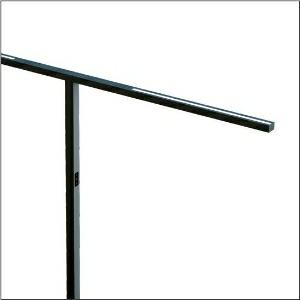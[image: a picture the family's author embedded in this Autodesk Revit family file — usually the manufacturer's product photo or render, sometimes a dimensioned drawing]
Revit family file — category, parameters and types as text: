
# Revit family: silica_31_floor_duo_51my52hmtcb
name_source: partatom
category: Lighting Fixtures
units: mm (PartAtom-declared; Revit-internal decimal feet)

## family parameters
Cut with Voids When Loaded = No
Host = Face
Light Source = No
Part Type = Normal
Room Calculation Point = No
Round Connector Dimension = Use Diameter
Shared = No

## types (1)
- --- (1 x LED, 17040 lm, 142 W, 4000K)
    Apparent Load = 142 VA
    CIE Flux Codes = 86 100 100 24 100
    Color Rendering = 80
    Color Temperature = 4000K
    Default Elevation = 1800 mm
    Description = Silica® 31 Floor duo, floorstanding luminaire, secondary optical cover: cover panel, of PMMA, light emission: direct/indirect distribution, primary light characteristic: symmetric, installation type: not mounted, LED, rated luminous flux: 17.040lm, luminous efficacy: 120lm/W, light colour: 8tw, colour temperature: 2700..6500K, control gear: Touchdim, daylight-dependent control, with cable with plug, mains connection: 230V, AC, 50Hz, connection cable included, cable length: 2,5m, rated input power: 142W, luminaire head, of aluminium, coated, jet black (RAL 9005), length: 2.372mm, width: 52mm, supporting column, angular, of aluminium, coated, jet black (RAL 9005), baseplate, of steel, coated, jet black (RAL 9005), local control - self-sufficient standalone sensors, direct and indirect component separately switchable, protection rating (complete): IP20, insulation class (complete): insulation class I (protective earthing), certification: CE, ENEC, permissible operating ambient temperature: -20..+40°C, standard: EN 50419, packaging unit: 1 piece
    Height = 36 mm
    Lamp = 1 x LED
    Lamp Light Flux = 17040 lm
    Lamp Power = 142 W
    Lamp count = 1
    Length = 2372 mm
    Luminous efficacy = 120 lm/W
    Manufacturer = Siteco
    ModVariant = No
    Model = 51MY52HMTCB
    Mounting Place = Floor
    Mounting Type = Freestanding
    Number of Poles = 1
    OnlyDefault = Yes
    Power Factor = 1
    Product Name = Silica 31 Floor duo
    Product group = floorstanding luminaire
    ProductGroupID = 1302
    Protection Class = Protection class I
    Protection Degree = IP 20
    RLX_Detail_Level = 1
    RLX_Emergency_Light_Flux = 0 lm
    RLX_Emergency_Type = 0
    RLX_Emergency_Type_DB = No
    RlxData = <blob elided: 21785 chars, md5=6ef24a2b>
    Socket = socket
    Standby Power = 0 W
    System Light Flux = 17040 lm
    System Power = 142 W
    Type Comments = factory setting
    Type Image = l_1275315.jpg
    URL = http://relux.com
    VarID = @adj_087111
    Voltage = 0 V
    Weight = 0.00 kg
    Width = 52 mm  [stored 0.170604 ft]

note: [stored X ft] marks values corroborated as IEEE doubles in the binary element streams (Revit-internal decimal feet)

## geometry (parser evidence)
native form markers: Blend x4, Sweep x14
no freeform markers — native parametric forms only
